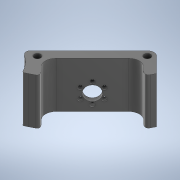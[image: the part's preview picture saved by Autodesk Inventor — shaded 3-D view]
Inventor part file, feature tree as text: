
AUTODESK INVENTOR PART (.ipt)
format: ipt  version: 2020 (Build 240168000, 168)  size: 381,952 bytes
history: native  units: mm
features: extrude x5, sketch x2, other x1, chamfer x1
ambient origin geometry x8: Origin, YZ Plane, XZ Plane, XY Plane, X Axis, Y Axis, Z Axis, Center Point
bodies: Body1 (feature_tree)
feature tree (9):
  other  "Твердое тело1"
  sketch  "Эскиз1"
  extrude  "Выдавливание10"  Depth=5.0mm
  extrude  "Выдавливание11"  Depth=6.0mm
  extrude  "Выдавливание12"  Depth=35.0mm TaperAngle=0.0deg
  sketch  "Эскиз6"
  extrude  "Выдавливание13"  Depth=31.5mm TaperAngle=0.0deg
  extrude  "Выдавливание14"  Depth=3.5mm TaperAngle=0.0deg
  chamfer  "Фаска3"  Distance=59.0mm
